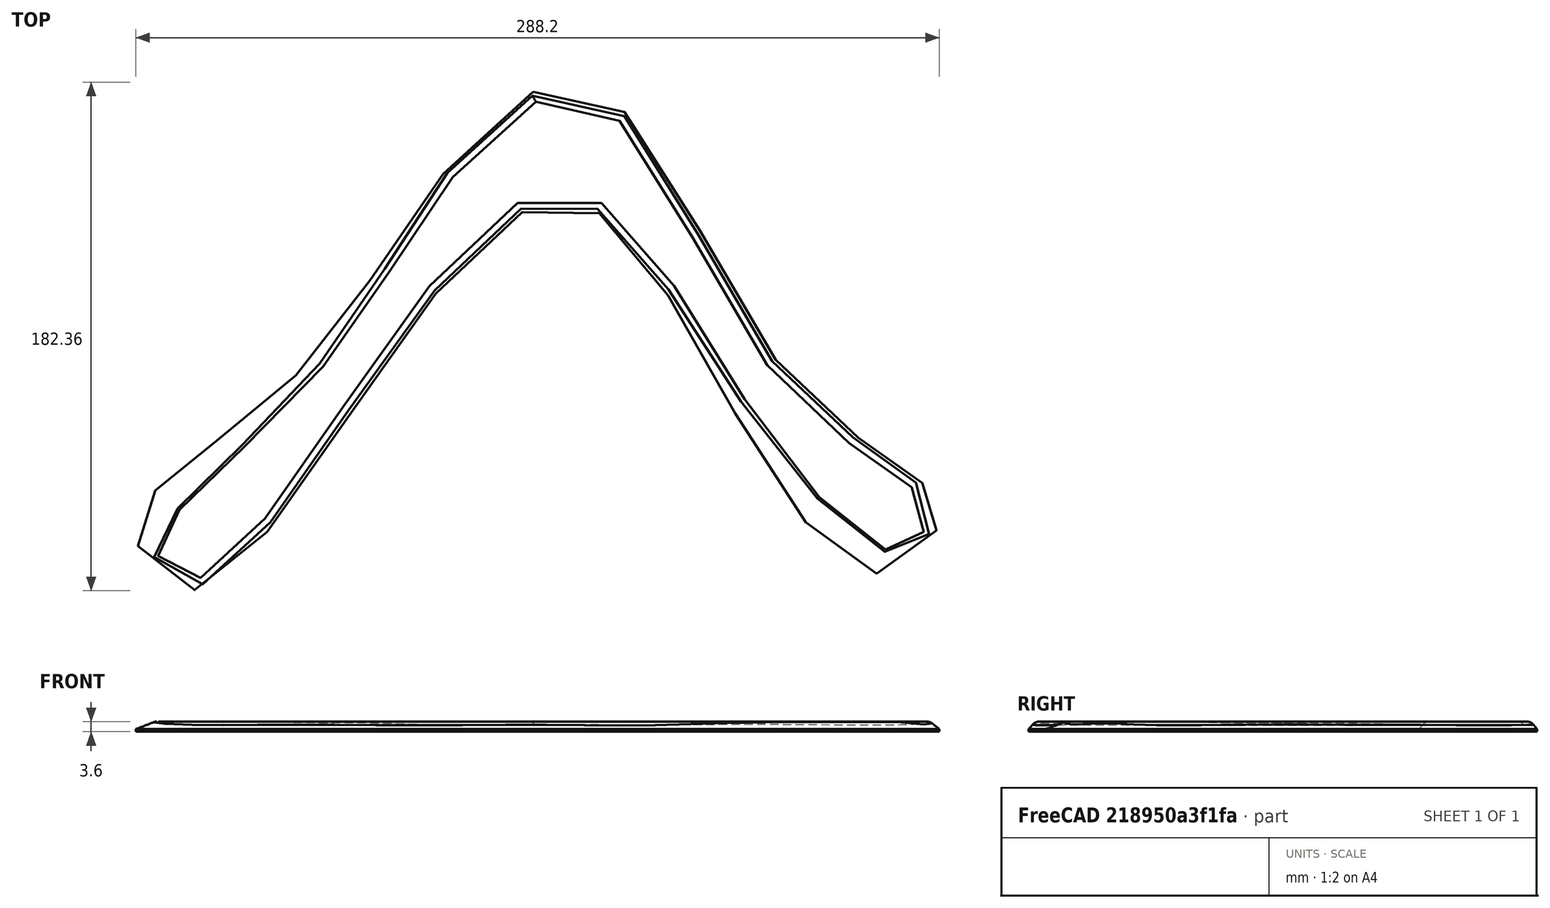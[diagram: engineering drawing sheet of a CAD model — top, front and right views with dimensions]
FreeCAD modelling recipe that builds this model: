
FCSTD DOCUMENT  (FreeCAD 1.2R46222 (Git))
Label: spline-1.2
License: All rights reserved
LicenseURL: https://en.wikipedia.org/wiki/All_rights_reserved
objects: Sketcher::SketchObject×2, App::Point×1, PartDesign::AdditiveLoft×1, PartDesign::Pad×1, PartDesign::Fillet×1, PartDesign::Body×1
note: 14 computed .brp shape members not serialized (recipe doc carries the construction recipe); baked Part::Feature solids carry a one-line shape summary decoded from their .brp

FEATURE [App::Point] Origin001  label="Origin-Point"
  Role = Origin
FEATURE [Sketcher::SketchObject] Sketch  label="Bottom Outline"
  ArcFitTolerance = 1e-06
  AttachmentSupport = -> [Origin]
  ExternalTypes = [0]
  FullyConstrained = false
  MakeInternals = true
  MapMode = 5
  _ExternalGeoVersion = 1
  sketch-geometry (27):
    g0-g11: GeomPoint [constr] x12 (B-spline internal-alignment scaffolding for g12; pole/knot coordinates omitted)
    g12: BSplineCurve PolesCount=13 KnotsCount=13 Degree=3 IsPeriodic=1
    g13-g25: Circle [constr] x13 (B-spline internal-alignment scaffolding for g12; pole/knot coordinates omitted)
    g26: GeomPoint [constr] X=-6.50685 Y=-0.939232 Z=0
  constraints (28):
    c: InternalAlignment(g0-g11 -> g12) x12
    c: InternalAlignment(g13,g12)
    c: Weight(g13) = 1
    c: InternalAlignment(g14,g12)
    c: Equal(g14,g13)
    c: InternalAlignment(g15,g12)
    c: Equal(g15,g13)
    c: InternalAlignment(g16,g12)
    c: Equal(g16,g13)
    c: InternalAlignment(g17,g12)
    c: Equal(g17,g13)
    c: InternalAlignment(g18,g12)
    c: Equal(g18,g13)
    c: InternalAlignment(g19,g12)
    c: Equal(g19,g13)
    c: InternalAlignment(g20,g12)
    c: Equal(g20,g13)
    c: InternalAlignment(g21,g12)
    c: Equal(g21,g13)
    c: InternalAlignment(g22,g12)
    c: Equal(g22,g13)
    c: InternalAlignment(g23,g12)
    c: Equal(g23,g13)
    c: InternalAlignment(g24,g12)
    c: Equal(g24,g13)
    c: InternalAlignment(g25,g12)
    c: Equal(g25,g13)
    c: InternalAlignment(g26,g12)
FEATURE [Sketcher::SketchObject] Sketch001  label="Top Outline"
  ArcFitTolerance = 1e-06
  AttachmentOffset = pos=(0,0,2.7) rot=(0,0,1;0rad)
  AttachmentSupport = -> [Sketch]
  ExternalTypes = [0]
  FullyConstrained = false
  MakeInternals = true
  MapMode = 2
  Placement = pos=(0,0,2.7) rot=(0,0,1;0rad)
  _ExternalGeoVersion = 1
  sketch-geometry (27):
    g0-g11: GeomPoint [constr] x12 (B-spline internal-alignment scaffolding for g12; pole/knot coordinates omitted)
    g12: BSplineCurve PolesCount=13 KnotsCount=13 Degree=3 IsPeriodic=1
    g13-g25: Circle [constr] x13 (B-spline internal-alignment scaffolding for g12; pole/knot coordinates omitted)
    g26: GeomPoint [constr] X=-7.03205 Y=-3.50675 Z=0
  constraints (28):
    c: InternalAlignment(g0-g11 -> g12) x12
    c: InternalAlignment(g13,g12)
    c: Weight(g13) = 1
    c: InternalAlignment(g14,g12)
    c: Equal(g14,g13)
    c: InternalAlignment(g15,g12)
    c: Equal(g15,g13)
    c: InternalAlignment(g16,g12)
    c: Equal(g16,g13)
    c: InternalAlignment(g17,g12)
    c: Equal(g17,g13)
    c: InternalAlignment(g18,g12)
    c: Equal(g18,g13)
    c: InternalAlignment(g19,g12)
    c: Equal(g19,g13)
    c: InternalAlignment(g20,g12)
    c: Equal(g20,g13)
    c: InternalAlignment(g21,g12)
    c: Equal(g21,g13)
    c: InternalAlignment(g22,g12)
    c: Equal(g22,g13)
    c: InternalAlignment(g23,g12)
    c: Equal(g23,g13)
    c: InternalAlignment(g24,g12)
    c: Equal(g24,g13)
    c: InternalAlignment(g25,g12)
    c: Equal(g25,g13)
    c: InternalAlignment(g26,g12)
FEATURE [PartDesign::AdditiveLoft] AdditiveLoft
  Closed = false
  Profile = -> Sketch
  Refine = true
  Ruled = false
  Sections = -> [Sketch001]
  Suppressed = false
FEATURE [PartDesign::Pad] Pad
  BaseFeature = -> AdditiveLoft
  Direction = (0,0,-1)
  Length = 0.9
  Length2 = 10
  Profile = -> AdditiveLoft [Face1]
  Refine = true
  SideType = 0
  Suppressed = false
  Type = 0
  Type2 = 0
FEATURE [PartDesign::Fillet] Fillet
  Base = -> Pad [Face3]
  BaseFeature = -> Pad
  Radius = 3
  Refine = true
  SupportTransform = false
  Suppressed = false
  UseAllEdges = false
FEATURE [PartDesign::Body] Body
  AllowCompound = true
  Group = -> [Sketch,Sketch001,AdditiveLoft,Pad,Fillet]
  Origin = -> Origin
  Tip = -> Fillet
